# Revit family: NBS_Schluter-SystemsLtd_WstesForShwrTrys_Schluter-KERDI-DRAIN
name_source: partatom
category: Plumbing Fixtures
revit_build: Autodesk Revit 2015 (Build: 20140606_1530(x64)
units: mm (PartAtom-declared; Revit-internal decimal feet)

## types (1)
- KDR10ED1
    AssetType = Fixed
    BIMObjectName = NBS_Schlüter-SystemsLtd_WastesForShowerTrays_Schlüter®-KERDI-DRAIN(KDBH50GV)-GrateAndFrameSet-KDR10ED1
    BodyMaterial = Drain body: High impact polypropylene (PP); Bonding flange insert: Acrylnitrile butadiene styrene (ABS); Schlüter®-KERDI collar: Polyethylene (PE) with a special fleece fabric laminated on both sides
    BondingFlangeDiameter = 300 mm
    BondingFlangeHeight = 152 mm
    Category = Pr_70_55_96_83:Shower tray wastes
    Color = silver
    CoverLength = 100 mm  [stored 0.328084 ft]
    CoverMaterial = Stainless steel V2A 1.4301
    CoverWidth = 100 mm  [stored 0.328084 ft]
    Description = Shower floor drain set with odour trap and stainless steel square shower grate
    DrainBodyHeight = 78 mm
    DrainageCapacity = DN 50 = 0.6 L/s (36 L/min) with DN 40 inlet
    DurationUnit = year
    Features = Bonding flange and the Schlüter®-KERDI collar which forms a secure, height adjustment ring, laterally adjustable in all directions
    Form = Flush square drain
    FrameHeight = 0 mm  [stored 0 ft]
    Grate = Design 1
    GrateAndFrameSet = NBS_Schluter-SystemsLtd_WstesForShwrTrys_GrateAndFrameSet_KDR10ED1
    GrateMaterial = NBS_Concept
    IfcExportAs = IfcWasteTerminalType
    IfcExportType = FLOORWASTE
    Manufacturer = www.schluter.co.uk
    ManufacturerName = Schlüter-Systems Ltd
    ManufacturerURL = www.schluter.co.uk
    ModelNumber = KD R10 ED1
    ModelReference = Schlüter®-KERDI-DRAIN (KD BH 50 GV) - Grate And Frame Set
    NBSCertification = www.nationalbimlibrary.com/cert/urb43les
    NBSDescription = Wastes for shower trays
    NBSReference = 45-35-70/337
    Name = WastesForShowerTrays_Schlüter®-KERDI-DRAIN(KDBH50GV)-GrateAndFrameSet-KDR10ED1_Schlüter-SystemsLtd
    NominalBodyDepth = 78 mm
    NominalBodyLength = 325 mm
    NominalBodyWidth = 230 mm
    NominalHeight = 0 mm  [stored 0 ft]
    NominalLength = 325 mm
    NominalWidth = 300 mm
    OutletConnectionSize = 50 mm  [stored 0.164042 ft]
    ProductInformation = www.schluter.co.uk<userpath>
    SealWaterLevel = 30 mm
    SuitableFrameCoverings = Ceramic tiles, natural stone and other coatings with thicknesses of 3-30 mm
    Uniclass2015Code = Pr_70_55_96_83
    Uniclass2015Title = Shower tray wastes
    Uniclass2015Version = Products v1.5
    Version = 2
    WarrantyDescription = 5 years (Please contact Schlüter-Systems for further warranty information)
    WarrantyDurationUnit = year

note: [stored X ft] marks values corroborated as IEEE doubles in the binary element streams (Revit-internal decimal feet)

## geometry (parser evidence)
native form markers: Sweep x23
no freeform markers — native parametric forms only
